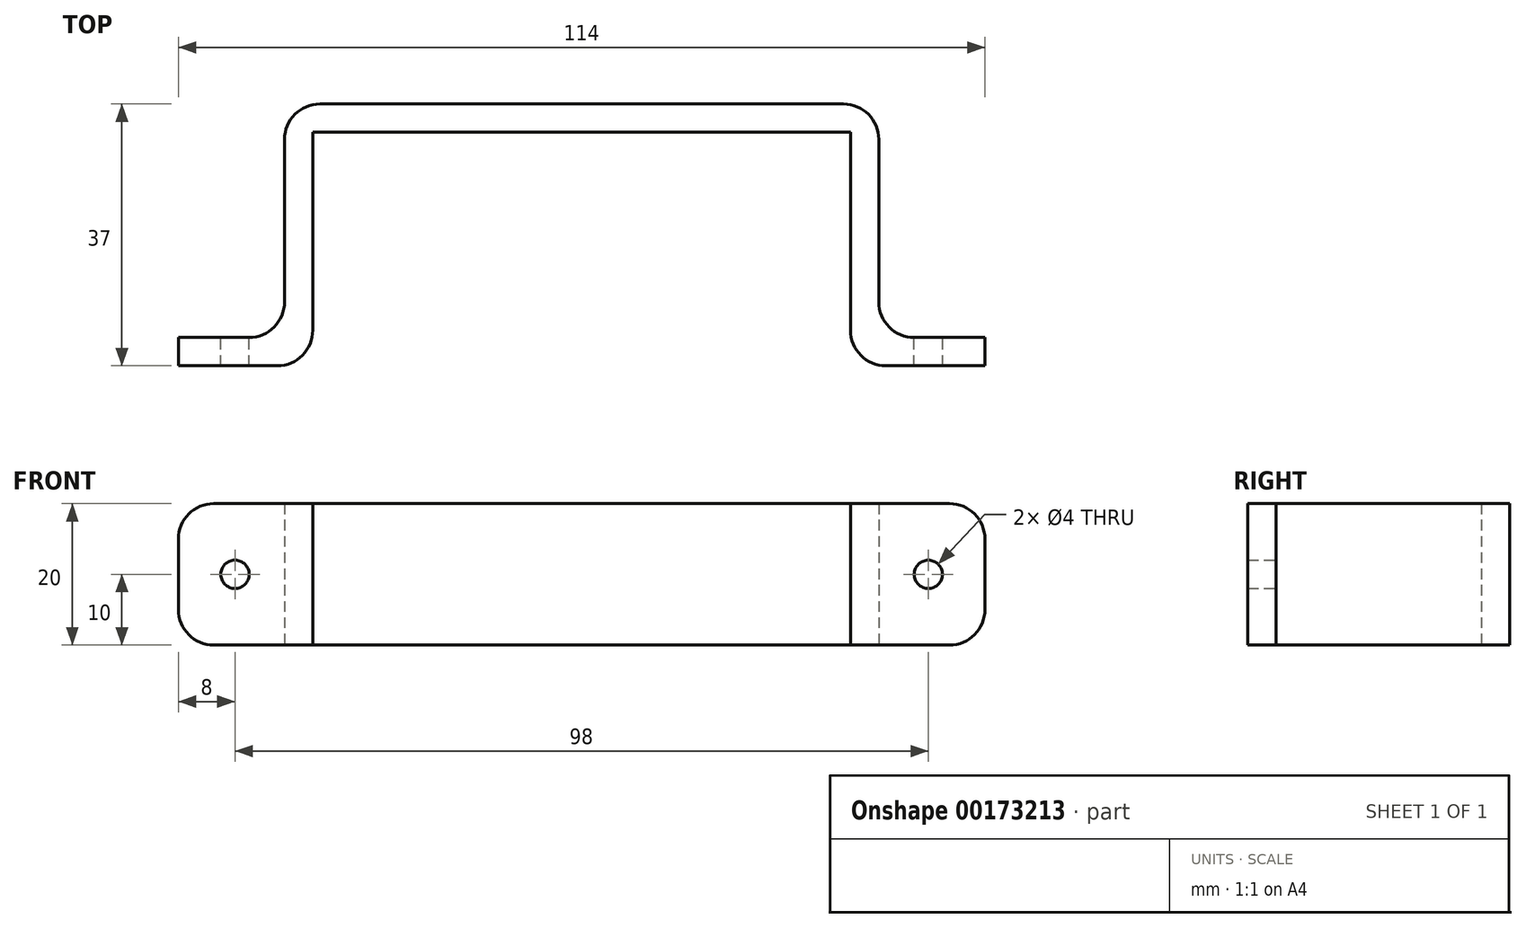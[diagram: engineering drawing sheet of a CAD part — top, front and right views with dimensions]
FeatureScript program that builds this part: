
annotation { "Feature Type Name" : "Feature", "Feature Type Description" : "" }
export const myFeature = defineFeature(function(context is Context, id is Id, definition is map)
    precondition{}
    {
        {
            var Q0;
            Q0=qCreatedBy(makeId("Top.planeOp"),FACE);
            var sketch = newSketch(context, id + "F0", { "sketchPlane" : qUnion([Q0])});
            skLineSegment(sketch, "E0", {"start": v(0, 33) * mm, "end": v(-38, 33) * mm});
            skLineSegment(sketch, "E1", {"start": v(-38, 33) * mm, "end": v(-38, 0) * mm});
            skLineSegment(sketch, "E2", {"start": v(-38, 0) * mm, "end": v(-57, 0) * mm});
            skLineSegment(sketch, "E3", {"start": v(-57, 0) * mm, "end": v(-57, 4) * mm});
            skLineSegment(sketch, "E4", {"start": v(-57, 4) * mm, "end": v(-42, 4) * mm});
            skLineSegment(sketch, "E5", {"start": v(-42, 4) * mm, "end": v(-42, 37) * mm});
            skLineSegment(sketch, "E6", {"start": v(-42, 37) * mm, "end": v(0, 37) * mm});
            skLineSegment(sketch, "E7", {"start": v(0, 37) * mm, "end": v(0, 33) * mm});
            skLineSegment(sketch, "E8.MirrorCS", {"start": v(42, 37) * mm, "end": v(0, 37) * mm});
            skLineSegment(sketch, "E9.MirrorCS", {"start": v(0, 33) * mm, "end": v(38, 33) * mm});
            skLineSegment(sketch, "E10.MirrorCS", {"start": v(38, 33) * mm, "end": v(38, 0) * mm});
            skLineSegment(sketch, "E11.MirrorCS", {"start": v(38, 0) * mm, "end": v(57, 0) * mm});
            skLineSegment(sketch, "E12.MirrorCS", {"start": v(57, 0) * mm, "end": v(57, 4) * mm});
            skLineSegment(sketch, "E13.MirrorCS", {"start": v(57, 4) * mm, "end": v(42, 4) * mm});
            skLineSegment(sketch, "E14.MirrorCS", {"start": v(42, 4) * mm, "end": v(42, 37) * mm});
            skSolve(sketch);
        }
        {
            var Q0;
            Q0=makeQuery(id+"F0.imprint","IMPRINT",FACE,{"disambiguationData":[TD([[makeQuery(id+"F0.imprint","IMPRINT",EDGE,{"derivedFrom":sQuery(id+"F0.wireOp",EDGE,"E0")}),-1.0]])]});
            var Q1;
            Q1=makeQuery(id+"F0.imprint","IMPRINT",FACE,{"disambiguationData":[TD([[makeQuery(id+"F0.imprint","IMPRINT",EDGE,{"derivedFrom":sQuery(id+"F0.wireOp",EDGE,"E7")}),1.0]])]});
            extrude(context, id + "F1", {"entities" : qUnion([Q0, Q1]), "depth" : 20 * mm});
        }
        {
            var Q0;
            Q0=makeQuery(id+"F1.opExtrude","SWEPT_FACE",FACE,{"disambiguationData":[OSD([sQuery(id+"F0.wireOp",EDGE,"E4")])]});
            var sketch = newSketch(context, id + "F2", { "sketchPlane" : qUnion([Q0])});
            skCircle(sketch, "E15", {"center": v(49, 10) * mm, "radius": 2 * mm});
            skCircle(sketch, "E16.MirrorC", {"center": v(-49, 10) * mm, "radius": 2 * mm});
            skSolve(sketch);
        }
        {
            var Q0;
            Q0 = qSketchRegion(id + "F2", true);
            extrude(context, id + "F3", {"entities" : qUnion([Q0]), "operationType" : NewBodyOperationType.REMOVE, "oppositeDirection" : true, "depth" : 25 * mm});
        }
        {
            var Q0;
            Q0=makeQuery(id+"F1.opExtrude","CAP_EDGE",EDGE,{"disambiguationData":[OSD([sQuery(id+"F0.wireOp",EDGE,"E3")])],"isStart":false});
            var Q1;
            Q1=makeQuery(id+"F1.opExtrude","CAP_EDGE",EDGE,{"disambiguationData":[OSD([sQuery(id+"F0.wireOp",EDGE,"E3")])],"isStart":true});
            var Q2;
            Q2=makeQuery(id+"F1.opExtrude","CAP_EDGE",EDGE,{"disambiguationData":[OSD([sQuery(id+"F0.wireOp",EDGE,"E12.MirrorCS")])],"isStart":true});
            var Q3;
            Q3=makeQuery(id+"F1.opExtrude","CAP_EDGE",EDGE,{"disambiguationData":[OSD([sQuery(id+"F0.wireOp",EDGE,"E12.MirrorCS")])],"isStart":false});
            var Q4;
            Q4=makeQuery(id+"F1.opExtrude","SWEPT_EDGE",EDGE,{"disambiguationData":[OSD([sQuery(id+"F0.wireOp",EDGE,"E8.MirrorCS"),sQuery(id+"F0.wireOp",EDGE,"E14.MirrorCS")])]});
            var Q5;
            Q5=makeQuery(id+"F1.opExtrude","SWEPT_EDGE",EDGE,{"disambiguationData":[OSD([sQuery(id+"F0.wireOp",EDGE,"E5"),sQuery(id+"F0.wireOp",EDGE,"E6")])]});
            var Q6;
            Q6=makeQuery(id+"F1.opExtrude","SWEPT_EDGE",EDGE,{"disambiguationData":[OSD([sQuery(id+"F0.wireOp",EDGE,"E1"),sQuery(id+"F0.wireOp",EDGE,"E2")])]});
            var Q7;
            Q7=makeQuery(id+"F1.opExtrude","SWEPT_EDGE",EDGE,{"disambiguationData":[OSD([sQuery(id+"F0.wireOp",EDGE,"E10.MirrorCS"),sQuery(id+"F0.wireOp",EDGE,"E11.MirrorCS")])]});
            var Q8;
            Q8=makeQuery(id+"F1.opExtrude","SWEPT_EDGE",EDGE,{"disambiguationData":[OSD([sQuery(id+"F0.wireOp",EDGE,"E13.MirrorCS"),sQuery(id+"F0.wireOp",EDGE,"E14.MirrorCS")])]});
            var Q9;
            Q9=makeQuery(id+"F1.opExtrude","SWEPT_EDGE",EDGE,{"disambiguationData":[OSD([sQuery(id+"F0.wireOp",EDGE,"E4"),sQuery(id+"F0.wireOp",EDGE,"E5")])]});
            fillet(context, id + "F4", {"entities" : qUnion([Q0, Q1, Q2, Q3, Q4, Q5, Q6, Q7, Q8, Q9]), "radius" : 5 * mm, "tangentPropagation" : true, "allowEdgeOverflow" : false});
        }
    });
